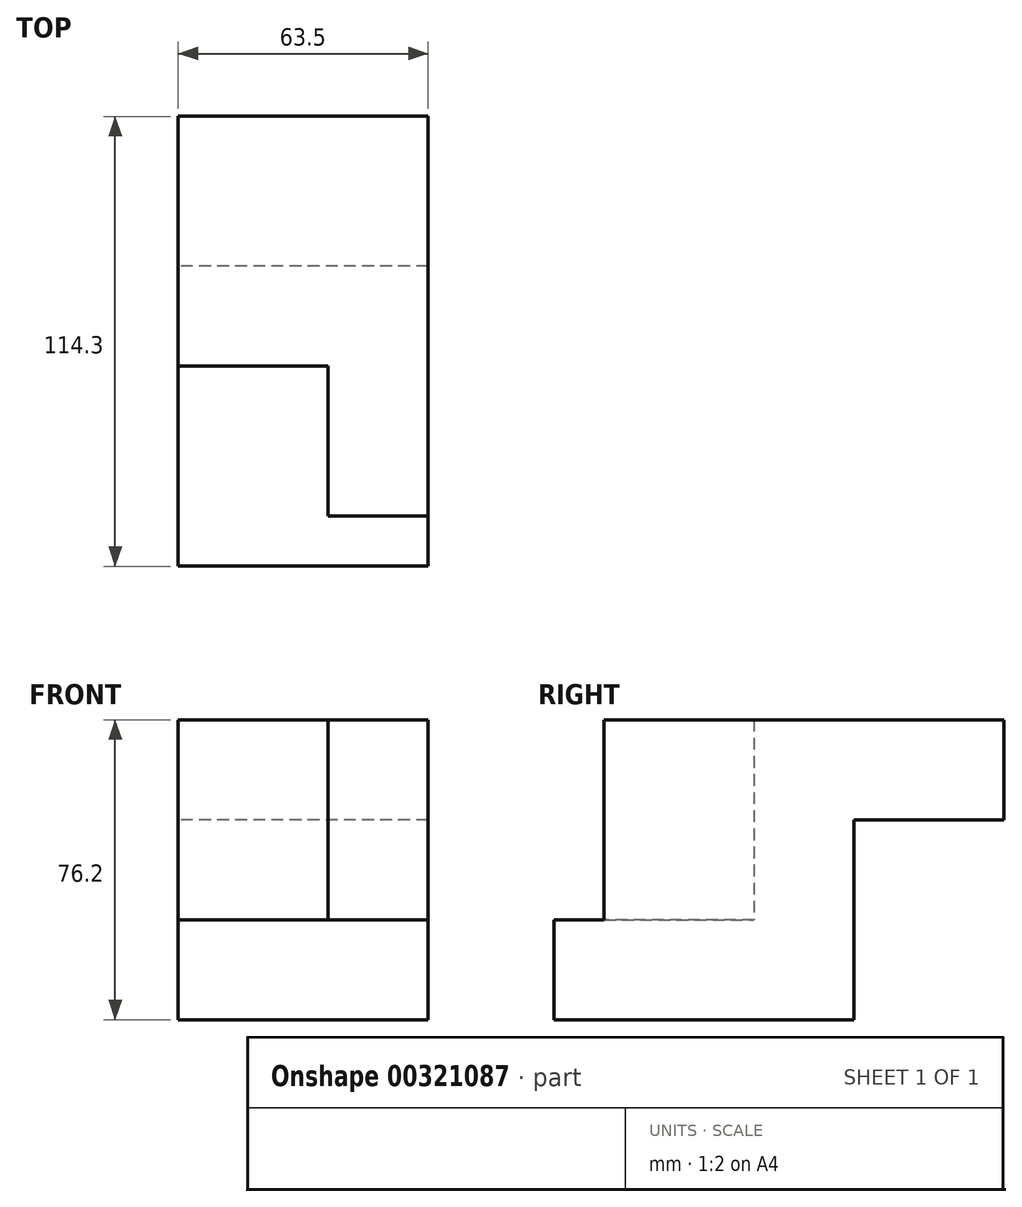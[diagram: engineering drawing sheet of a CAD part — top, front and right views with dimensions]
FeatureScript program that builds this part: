
annotation { "Feature Type Name" : "Feature", "Feature Type Description" : "" }
export const myFeature = defineFeature(function(context is Context, id is Id, definition is map)
    precondition{}
    {
        {
            var Q0;
            Q0=qCreatedBy(makeId("Right.planeOp"),FACE);
            var sketch = newSketch(context, id + "F0", { "sketchPlane" : qUnion([Q0])});
            skLineSegment(sketch, "E0", {"start": v(45.75, 45.68) * mm, "end": v(-17.75, 45.68) * mm});
            skLineSegment(sketch, "E1", {"start": v(-17.75, 45.68) * mm, "end": v(-17.75, -5.12) * mm});
            skLineSegment(sketch, "E2", {"start": v(-17.75, -5.12) * mm, "end": v(-68.55, -5.12) * mm});
            skLineSegment(sketch, "E3", {"start": v(-68.55, -5.12) * mm, "end": v(-68.55, -30.52) * mm});
            skLineSegment(sketch, "E4", {"start": v(-68.55, -30.52) * mm, "end": v(7.65, -30.52) * mm});
            skLineSegment(sketch, "E5", {"start": v(7.65, -30.52) * mm, "end": v(7.65, 20.28) * mm});
            skLineSegment(sketch, "E6", {"start": v(7.65, 20.28) * mm, "end": v(45.75, 20.28) * mm});
            skLineSegment(sketch, "E7", {"start": v(45.75, 20.28) * mm, "end": v(45.75, 45.68) * mm});
            skSolve(sketch);
        }
        {
            var Q0;
            Q0=makeQuery(id+"F0.imprint","IMPRINT",FACE,{"disambiguationData":[TD([[makeQuery(id+"F0.imprint","IMPRINT",EDGE,{"derivedFrom":sQuery(id+"F0.wireOp",EDGE,"E0")}),1.0]])]});
            extrude(context, id + "F1", {"entities" : qUnion([Q0]), "depth" : 63.5 * mm});
        }
        {
            var Q0;
            Q0=makeQuery(id+"F1.opExtrude","SWEPT_FACE",FACE,{"disambiguationData":[OSD([sQuery(id+"F0.wireOp",EDGE,"E1")])]});
            var sketch = newSketch(context, id + "F2", { "sketchPlane" : qUnion([Q0])});
            skLineSegment(sketch, "E8.bottom", {"start": v(63.5, 45.68) * mm, "end": v(38.1, 45.68) * mm});
            skLineSegment(sketch, "E8.top", {"start": v(63.5, -5.12) * mm, "end": v(38.1, -5.12) * mm});
            skLineSegment(sketch, "E8.left", {"start": v(63.5, 45.68) * mm, "end": v(63.5, -5.12) * mm});
            skLineSegment(sketch, "E8.right", {"start": v(38.1, 45.68) * mm, "end": v(38.1, -5.12) * mm});
            skSolve(sketch);
        }
        {
            var Q0;
            Q0=makeQuery(id+"F2.imprint","IMPRINT",FACE,{"disambiguationData":[TD([[makeQuery(id+"F2.imprint","IMPRINT",EDGE,{"derivedFrom":sQuery(id+"F2.wireOp",EDGE,"E8.bottom")}),1.0]])]});
            extrude(context, id + "F3", {"entities" : qUnion([Q0]), "operationType" : NewBodyOperationType.ADD, "depth" : 38.1 * mm});
        }
    });
